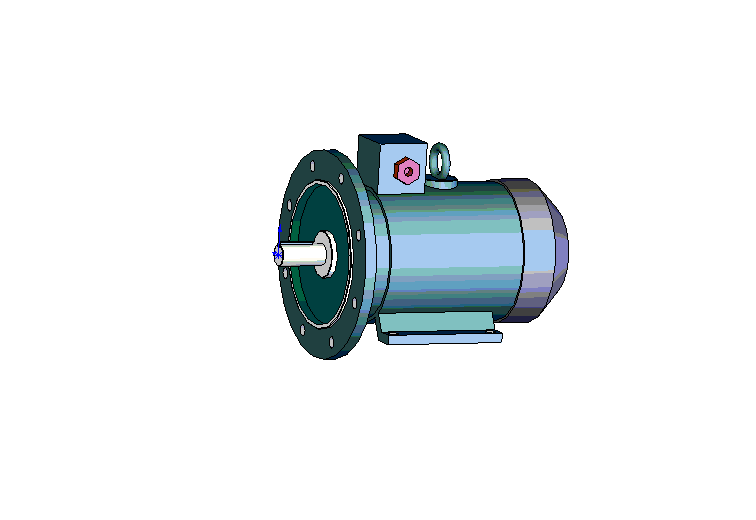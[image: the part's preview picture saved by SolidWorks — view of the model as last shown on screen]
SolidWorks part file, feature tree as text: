
SOLIDWORKS PART (.sldprt)
format: sldprt  version: not decoded by parser v0  size: 675,328 bytes
history: native  units: mm
features: sketch x18, extrude x12, plane x4, cut_extrude x4, chamfer x3, material x1, sweep x1 (+10 scaffold rows collapsed)
feature tree (53):
  scaffold x10  (default folders/planes/origin — collapsed)
  material  "Ст.3 ГОСТ 380-88"
  plane  "Спереди"
  plane  "Сверху"
  plane  "Справа"
  sketch  "Эскиз1"  dims[D1=38.0mm]
  extrude  "Вытянуть1"  Depth=80mm
  sketch  "Эскиз2"  dims[D1=8.0mm D2=8.0mm D3=41.0mm]
  extrude  "Вытянуть2"  Depth=60mm
  sketch  "Эскиз3"  dims[D1=350.0mm]
  extrude  "Вытянуть3"  Depth=19mm
  sketch  "Эскиз4"  dims[D1=250.0mm D2=236.0mm]
  extrude  "Вытянуть4"  Depth=5mm
  sketch  "Эскиз5"  dims[D1=236.0mm D2=80.0mm]
  cut_extrude  "Вырез-Вытянуть1"  Depth=10mm
  chamfer  "Фаска1"  Distance=1mm Angle=45deg
  sketch  "Эскиз6"  dims[c1.D2=19.0mm c1.D1=~202.320481mm c2.D1=22.5deg c2.D3=150.0mm c2.D4=150.0mm c2.D5=150.0mm]
  cut_extrude  "Вырез-Вытянуть2"  [1 undecoded]
  sketch  "Эскиз7"  dims[D1=220.0mm]
  extrude  "Вытянуть5"  Depth=55mm
  sketch  "Эскиз8"  dims[D1=232.0mm]
  extrude  "Вытянуть6"  Depth=242mm
  sketch  "Эскиз9"  dims[D1=240.0mm]
  extrude  "Вытянуть7"  Depth=102mm
  chamfer  "Фаска2"  Distance=45mm Angle=45deg
  sketch  "Эскиз10"  dims[c1.D1=16.0mm c1.D2=16.0mm c1.D3=~78.208589mm c2.D3=30.0deg c2.D4=123.0mm c2.D5=30.0mm c2.D6=132.0mm c2.D7=105.0mm]
  extrude  "Вытянуть8"  Depth=208mm
  sketch  "Эскиз11"  dims[c1.D2=19.0mm c1.D1=169.0mm c1.D3=108.0mm c1.D4=90.0deg c1.D5=309.0mm c1.D6=216.0mm c1.D7=178.0mm c2.D5=347.0mm c2.D6=~140.862792deg]
  cut_extrude  "Вырез-Вытянуть3"  [1 undecoded]
  sketch  "Эскиз12"  dims[D1=1.0mm D2=86.0mm D3=86.0mm]
  extrude  "Вытянуть9"  Depth=193mm
  sketch  "Эскиз13"  dims[D1=64.0mm D2=286.0mm]
  extrude  "Вытянуть10"  Depth=126mm
  chamfer  "Фаска3"  Distance=1mm Angle=45deg
  plane  "Плоскость1"  Offset=286mm
  sketch  "Эскиз14"  dims[D1=52.0mm]
  sketch  "Эскиз15"  dims[D1=14.0mm D2=52.0mm]
  sweep  "По траектории1"
  sketch  "Эскиз16"  dims[D1=30.0mm D2=43.0mm D3=43.0mm]
  extrude  "Вытянуть11"  Depth=10mm
  sketch  "Эскиз17"  dims[D1=19.5mm]
  extrude  "Вытянуть12"  Depth=15mm
  sketch  "Эскиз18"  dims[D1=16.0mm]
  cut_extrude  "Вырез-Вытянуть4"  Depth=15mm
decode coverage: 35 of 38 modeling features carry decoded parameters
note: ~ marks probable driven/reference dimensions
note: 2 parameter values undecoded
note: suppression state not decoded; provenance and decode notes live in map.json
